# Revit family: P210059AX-005_NFW5800HW
name_source: partatom
category: Specialty Equipment
units: mm (PartAtom-declared; Revit-internal decimal feet)

## family parameters
Always vertical = Yes
Cut with Voids When Loaded = No
Enable Cutting in Views = No
Maintain Annotation Orientation = No
Part Type = Normal
Room Calculation Point = No
Round Connector Dimension = Use Diameter
Shared = No
Work Plane-Based = No

## types (1)
- NFW5800HW
    Amps = 0 A
    Back Panel Material = ARCAT - Metal - Aluminum
    Body Material = ARCAT - Metal - White
    Button Panal Material = ARCAT - Plastic - White
    Clearance Material = ARCAT - Clearance
    Default Elevation = 0"
    Depth = 31 9/16"
    Description = 4.3 cu. ft. Front-Load Washer with Large Capacity
Laveuse à chargement frontal à profondeur de comptoir 5.0 pi³
    Dimension Guide = http://whirlpool.com
http://whirlpool.com
    Display Material = ARCAT - Plastic - Black
    Door Material = ARCAT - Metal - White
    Dsiplay Panel Material = ARCAT - Glass Tempered - Black
    Energy Guide = https://whirlpool.com
https://whirlpool.com
    Family Name = Front Load Washer
    Feature 1 = Large Capacity
Grande capacité
    Feature 2 = Wash System
Wash System
    Feature 3 = Automatic Fabric Softener Dispenser
Automatic Fabric Softener Dispenser
    Glass Material = ARCAT - Glass Tempered - Clear
    Height = 38 5/8"
    Installation-Fabrication = https://www.whirlpool.com
https://www.whirlpool.com
    Leg Material = ARCAT - Plastic - White
    Manufacturer = Whirlpool
    Model = NFW5800HW
    Voltage = 0 V
    Width = 27"

## geometry (parser evidence)
native form markers: Sweep x5
no freeform markers — native parametric forms only
